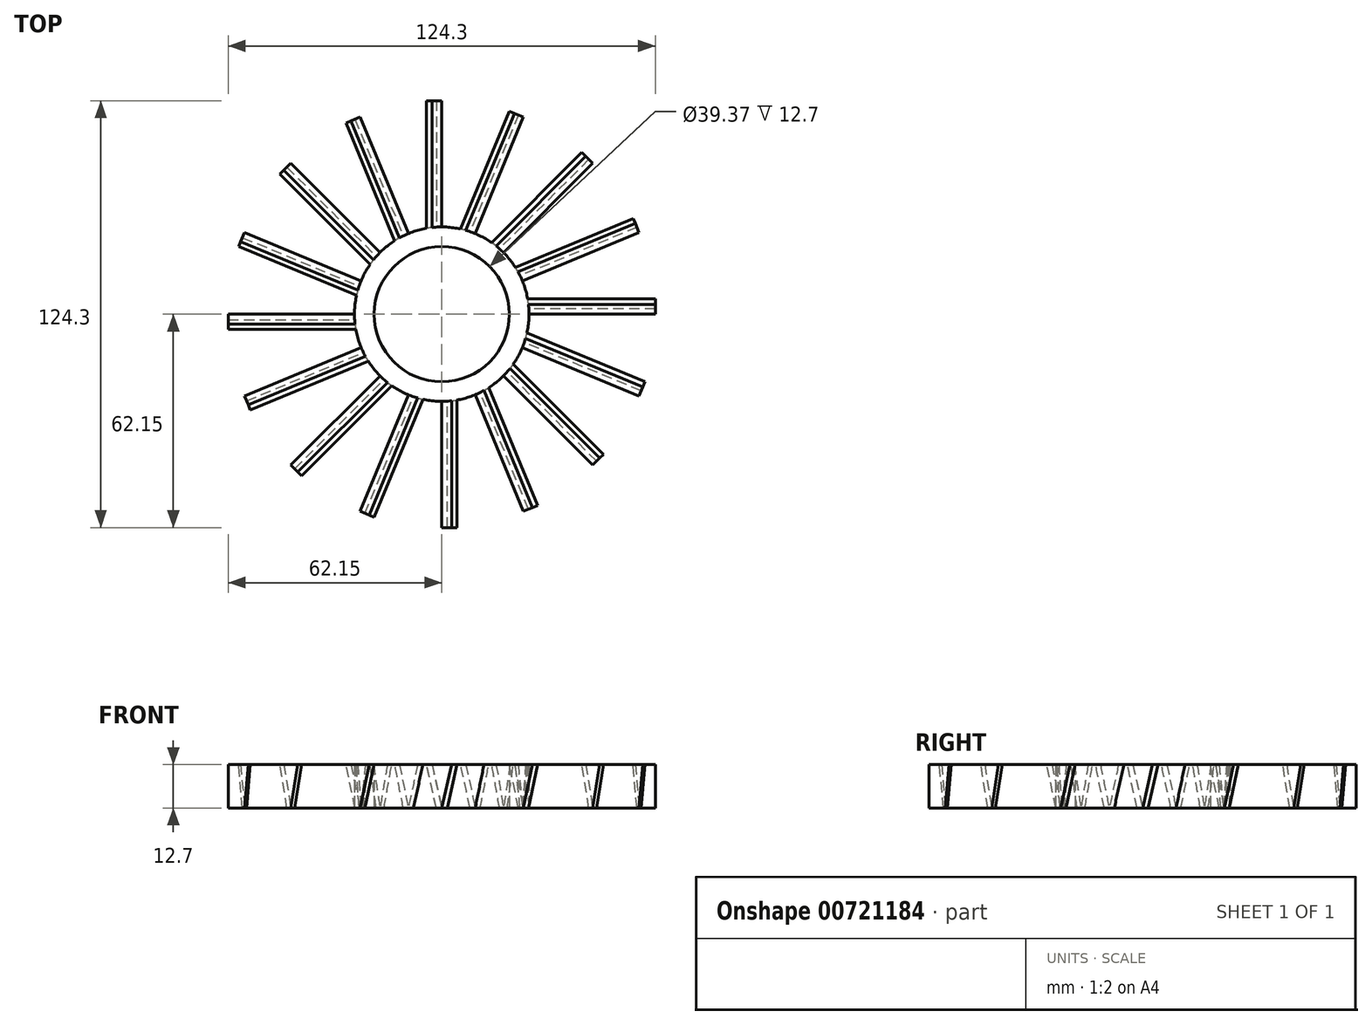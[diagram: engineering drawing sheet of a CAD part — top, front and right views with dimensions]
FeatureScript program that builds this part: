
annotation { "Feature Type Name" : "Feature", "Feature Type Description" : "" }
export const myFeature = defineFeature(function(context is Context, id is Id, definition is map)
    precondition{}
    {
        {
            var Q0;
            Q0=qCreatedBy(makeId("Top.planeOp"),FACE);
            var sketch = newSketch(context, id + "F0", { "sketchPlane" : qUnion([Q0])});
            skCircle(sketch, "E0", {"center": v(0, 0) * mm, "radius": 25.4 * mm});
            skCircle(sketch, "E1", {"center": v(0, 0) * mm, "radius": 19.69 * mm});
            skSolve(sketch);
        }
        {
            var Q0;
            Q0=makeQuery(id+"F0.imprint","IMPRINT",FACE,{"disambiguationData":[TD([[makeQuery(id+"F0.imprint","IMPRINT",EDGE,{"derivedFrom":sQuery(id+"F0.wireOp",EDGE,"E0")}),1.0]])]});
            extrude(context, id + "F1", {"entities" : qUnion([Q0]), "depth" : 12.7 * mm, "offsetDistance" : 25.4 * mm});
        }
        {
            var Q0;
            Q0=qCreatedBy(makeId("Front.planeOp"),FACE);
            var sketch = newSketch(context, id + "F2", { "sketchPlane" : qUnion([Q0])});
            skLineSegment(sketch, "E2", {"start": v(0, 0) * mm, "end": v(0, 0) * mm});
            skLineSegment(sketch, "E3", {"start": v(6.6, 12.7) * mm, "end": v(6.6, 12.7) * mm});
            skLineSegment(sketch, "E4", {"start": v(2.86, 12.7) * mm, "end": v(0, 0) * mm});
            skLineSegment(sketch, "E5", {"start": v(1.59, 0) * mm, "end": v(4.44, 12.7) * mm});
            skLineSegment(sketch, "E6", {"start": v(4.44, 12.7) * mm, "end": v(2.86, 12.7) * mm});
            skLineSegment(sketch, "E7", {"start": v(0, 0) * mm, "end": v(1.59, 0) * mm});
            skSolve(sketch);
        }
        {
            var Q0;
            Q0 = qSketchRegion(id + "F2", true);
            extrude(context, id + "F3", {"entities" : qUnion([Q0]), "depth" : 62.15 * mm, "offsetDistance" : 25.4 * mm, "hasSecondDirection" : true, "secondDirectionOppositeDirection" : false, "secondDirectionDepth" : 23.72 * mm});
        }
        {
            var Q0;
            Q0=makeQuery(id+"F3.opExtrude","SWEPT_BODY",BODY,{"disambiguationData":[OSD([sQuery(id+"F2.wireOp",EDGE,"E4"),sQuery(id+"F2.wireOp",EDGE,"E5"),sQuery(id+"F2.wireOp",EDGE,"E6"),sQuery(id+"F2.wireOp",EDGE,"E7")])]});
            var Q1;
            Q1=makeQuery(id+"F1.opExtrude","CAP_EDGE",EDGE,{"disambiguationData":[OSD([sQuery(id+"F0.wireOp",EDGE,"E1")])],"isStart":false});
            circularPattern(context, id + "F4", {"operationType" : NewBodyOperationType.ADD, "entities" : qUnion([Q0]), "axis" : qUnion([Q1]), "angle" : 360 * degree, "instanceCount" : 16, "equalSpace" : true});
        }
    });
